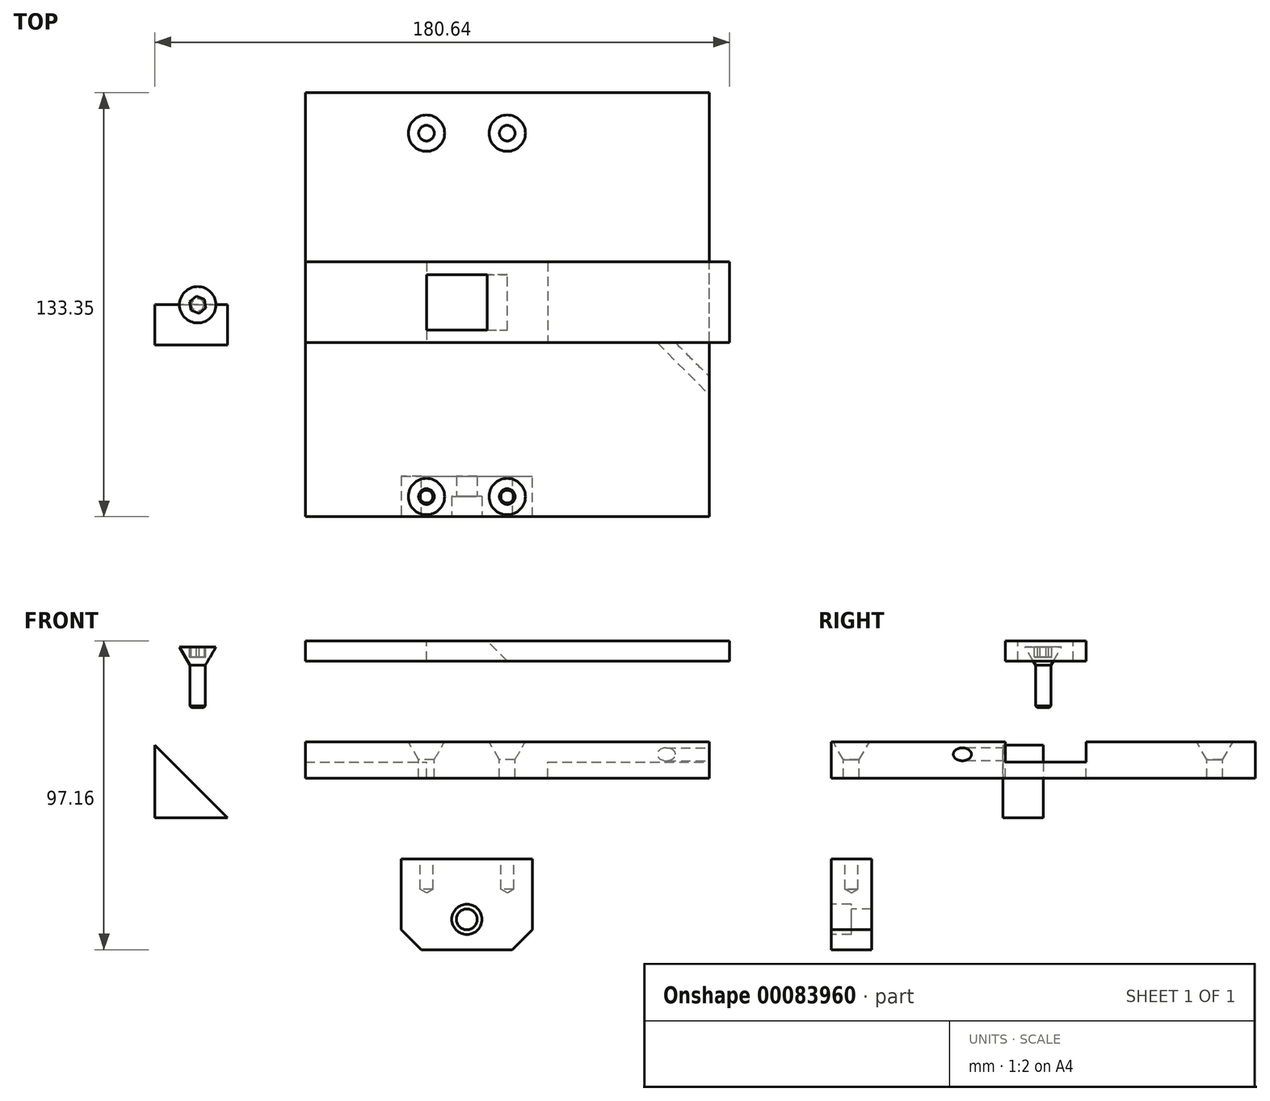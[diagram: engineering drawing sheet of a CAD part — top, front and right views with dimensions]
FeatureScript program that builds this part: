
annotation { "Feature Type Name" : "Feature", "Feature Type Description" : "" }
export const myFeature = defineFeature(function(context is Context, id is Id, definition is map)
    precondition{}
    {
        {
            var Q0;
            Q0=qCreatedBy(makeId("Top.planeOp"),FACE);
            var sketch = newSketch(context, id + "F0", { "sketchPlane" : qUnion([Q0])});
            skLineSegment(sketch, "E0.bottom", {"start": v(50.8, -66.68) * mm, "end": v(-50.8, -66.68) * mm});
            skLineSegment(sketch, "E0.top", {"start": v(50.8, 66.68) * mm, "end": v(-50.8, 66.68) * mm});
            skLineSegment(sketch, "E0.left", {"start": v(50.8, -66.68) * mm, "end": v(50.8, 66.68) * mm});
            skLineSegment(sketch, "E0.right", {"start": v(-50.8, -66.68) * mm, "end": v(-50.8, 66.68) * mm});
            skPoint(sketch, "E0.middle", {"position": v(0, 0) * mm});
            skSolve(sketch);
        }
        {
            var Q0;
            Q0=makeQuery(id+"F0.imprint","IMPRINT",FACE,{"disambiguationData":[TD([[makeQuery(id+"F0.imprint","IMPRINT",EDGE,{"derivedFrom":sQuery(id+"F0.wireOp",EDGE,"E0.bottom")}),-1.0]])]});
            extrude(context, id + "F1", {"entities" : qUnion([Q0]), "depth" : 11.43 * mm});
        }
        {
            var Q0;
            Q0=makeQuery(id+"F1.opExtrude","CAP_FACE",FACE,{"disambiguationData":[OSD([sQuery(id+"F0.wireOp",EDGE,"E0.bottom"),sQuery(id+"F0.wireOp",EDGE,"E0.top"),sQuery(id+"F0.wireOp",EDGE,"E0.left"),sQuery(id+"F0.wireOp",EDGE,"E0.right")])],"isStart":false});
            var sketch = newSketch(context, id + "F2", { "sketchPlane" : qUnion([Q0])});
            skLineSegment(sketch, "E1", {"start": v(-50.8, 53.98) * mm, "end": v(50.8, 53.98) * mm, "construction": true});
            skLineSegment(sketch, "E2", {"start": v(-50.8, -60.33) * mm, "end": v(50.8, -60.33) * mm, "construction": true});
            skLineSegment(sketch, "E3", {"start": v(-12.7, 66.68) * mm, "end": v(-12.7, -66.68) * mm, "construction": true});
            skLineSegment(sketch, "E4", {"start": v(12.7, 66.68) * mm, "end": v(12.7, -66.68) * mm, "construction": true});
            skPoint(sketch, "E5", {"position": v(-12.7, 53.98) * mm});
            skPoint(sketch, "E6", {"position": v(12.7, 53.98) * mm});
            skPoint(sketch, "E7", {"position": v(12.7, -60.33) * mm});
            skPoint(sketch, "E8", {"position": v(-12.7, -60.33) * mm});
            skSolve(sketch);
        }
        {
            var Q0;
            Q0=sQuery(id+"F2.wireOp",VERTEX,"E5");
            var Q1;
            Q1=sQuery(id+"F2.wireOp",VERTEX,"E6");
            var Q2;
            Q2=sQuery(id+"F2.wireOp",VERTEX,"E8");
            var Q3;
            Q3=sQuery(id+"F2.wireOp",VERTEX,"E7");
            var Q4;
            Q4=makeQuery(id+"F1.opExtrude","SWEPT_BODY",BODY,{"disambiguationData":[OSD([sQuery(id+"F0.wireOp",EDGE,"E0.bottom"),sQuery(id+"F0.wireOp",EDGE,"E0.top"),sQuery(id+"F0.wireOp",EDGE,"E0.left"),sQuery(id+"F0.wireOp",EDGE,"E0.right")])]});
            hole(context, id + "F3", {"style" : HoleStyle.C_SINK, "endStyle" : HoleEndStyle.THROUGH, "standardTappedOrClearance" : lookupTablePath({ "standard" : "ANSI", "size" : "#10 (0.2)", "type" : "Drilled" }), "standardBlindInLast" : lookupTablePath({ "standard" : "ANSI", "size" : "#10", "type" : "Drilled" }), "holeDiameter" : 4.9 * mm, "cSinkDiameter" : 11.43 * mm, "cSinkAngle" : 60 * degree, "locations" : qUnion([Q0, Q1, Q2, Q3]), "scope" : qUnion([Q4]), "isTappedThrough" : true});
        }
        {
            var Q0;
            Q0=makeQuery(id+"F1.opExtrude","CAP_FACE",FACE,{"disambiguationData":[OSD([sQuery(id+"F0.wireOp",EDGE,"E0.bottom"),sQuery(id+"F0.wireOp",EDGE,"E0.top"),sQuery(id+"F0.wireOp",EDGE,"E0.left"),sQuery(id+"F0.wireOp",EDGE,"E0.right")])],"isStart":true});
            cPlane(context, id + "F4", {"entities" : qUnion([Q0]), "cplaneType" : CPlaneType.OFFSET, "offset" : 25.4 * mm, "width" : 152.4 * mm, "height" : 152.4 * mm});
        }
        {
            var Q0;
            Q0=qCreatedBy(id+"F4.planeOp",FACE);
            var sketch = newSketch(context, id + "F5", { "sketchPlane" : qUnion([Q0])});
            skLineSegment(sketch, "E9.bottom", {"start": v(-20.64, 66.68) * mm, "end": v(20.64, 66.68) * mm});
            skLineSegment(sketch, "E9.top", {"start": v(-20.64, 53.98) * mm, "end": v(20.64, 53.98) * mm});
            skLineSegment(sketch, "E9.left", {"start": v(-20.64, 66.68) * mm, "end": v(-20.64, 53.98) * mm});
            skLineSegment(sketch, "E9.right", {"start": v(20.64, 66.68) * mm, "end": v(20.64, 53.98) * mm});
            skLineSegment(sketch, "E10", {"start": v(0, 66.68) * mm, "end": v(0, 53.98) * mm, "construction": true});
            skLineSegment(sketch, "E11", {"start": v(0, 66.68) * mm, "end": v(0, 24.97) * mm, "construction": true});
            skSolve(sketch);
        }
        {
            var Q0;
            Q0=makeQuery(id+"F5.imprint","IMPRINT",FACE,{"disambiguationData":[TD([[makeQuery(id+"F5.imprint","IMPRINT",EDGE,{"derivedFrom":sQuery(id+"F5.wireOp",EDGE,"E9.bottom")}),-1.0]])]});
            extrude(context, id + "F6", {"entities" : qUnion([Q0]), "depth" : 28.57 * mm});
        }
        {
            var Q0;
            Q0=qCreatedBy(id+"F4.planeOp",FACE);
            var sketch = newSketch(context, id + "F7", { "sketchPlane" : qUnion([Q0])});
            skPoint(sketch, "E12.0", {"position": v(-12.7, 60.33) * mm});
            skPoint(sketch, "E13.0", {"position": v(12.7, 60.33) * mm});
            skSolve(sketch);
        }
        {
            var Q0;
            Q0=sQuery(id+"F7.wireOp",VERTEX,"E12.0");
            var Q1;
            Q1=sQuery(id+"F7.wireOp",VERTEX,"E13.0");
            var Q2;
            Q2=makeQuery(id+"F6.opExtrude","SWEPT_BODY",BODY,{"disambiguationData":[OSD([sQuery(id+"F5.wireOp",EDGE,"E9.bottom"),sQuery(id+"F5.wireOp",EDGE,"E9.top"),sQuery(id+"F5.wireOp",EDGE,"E9.left"),sQuery(id+"F5.wireOp",EDGE,"E9.right")])]});
            hole(context, id + "F8", {"style" : HoleStyle.SIMPLE, "endStyle" : HoleEndStyle.BLIND, "oppositeDirection" : true, "standardTappedOrClearance" : lookupTablePath({ "standard" : "ANSI", "engagement" : "75%", "pitch" : "32 tpi", "size" : "#10", "type" : "Tapped" }), "standardBlindInLast" : lookupTablePath({ "standard" : "ANSI", "engagement" : "75%", "pitch" : "32 tpi", "size" : "#10", "type" : "Tapped" }), "holeDiameter" : 4.04 * mm, "holeDepth" : 9.52 * mm, "locations" : qUnion([Q0, Q1]), "scope" : qUnion([Q2]), "majorDiameter" : 4.83 * mm});
        }
        {
            var Q0;
            Q0=makeQuery(id+"F6.opExtrude","SWEPT_FACE",FACE,{"disambiguationData":[OSD([sQuery(id+"F5.wireOp",EDGE,"E9.bottom")])]});
            var sketch = newSketch(context, id + "F9", { "sketchPlane" : qUnion([Q0])});
            skLineSegment(sketch, "E14", {"start": v(0, -25.4) * mm, "end": v(0, -53.98) * mm, "construction": true});
            skLineSegment(sketch, "E15", {"start": v(-20.64, -44.44) * mm, "end": v(20.64, -44.44) * mm, "construction": true});
            skPoint(sketch, "E16", {"position": v(0, -44.44) * mm});
            skSolve(sketch);
        }
        {
            var Q0;
            Q0=sQuery(id+"F9.wireOp",VERTEX,"E16");
            var Q1;
            Q1=makeQuery(id+"F6.opExtrude","SWEPT_BODY",BODY,{"disambiguationData":[OSD([sQuery(id+"F5.wireOp",EDGE,"E9.bottom"),sQuery(id+"F5.wireOp",EDGE,"E9.top"),sQuery(id+"F5.wireOp",EDGE,"E9.left"),sQuery(id+"F5.wireOp",EDGE,"E9.right")])]});
            hole(context, id + "F10", {"style" : HoleStyle.C_BORE, "endStyle" : HoleEndStyle.THROUGH, "holeDiameter" : 6.53 * mm, "cBoreDiameter" : 9.52 * mm, "cBoreDepth" : 6.35 * mm, "locations" : qUnion([Q0]), "scope" : qUnion([Q1]), "isTappedThrough" : true});
        }
        {
            var Q0;
            Q0=makeQuery(id+"F2.imprint","IMPRINT",FACE,{"disambiguationData":[TD([[makeQuery(id+"F2.imprint","IMPRINT",EDGE,{"derivedFrom":makeQuery(id+"F1.opExtrude","CAP_EDGE",EDGE,{"disambiguationData":[OSD([sQuery(id+"F0.wireOp",EDGE,"E0.bottom")])],"isStart":false})}),-1.0]])]});
            var sketch = newSketch(context, id + "F11", { "sketchPlane" : qUnion([Q0])});
            skLineSegment(sketch, "E17.0.0", {"start": v(-12.7, -66.68) * mm, "end": v(12.7, -66.68) * mm, "construction": true});
            skCircle(sketch, "E17.0.1", {"center": v(12.7, -60.33) * mm, "radius": 5.71 * mm, "construction": true});
            skLineSegment(sketch, "E17.0.2", {"start": v(12.7, -66.68) * mm, "end": v(50.8, -66.68) * mm, "construction": true});
            skLineSegment(sketch, "E17.0.3", {"start": v(50.8, -66.68) * mm, "end": v(50.8, 66.68) * mm, "construction": true});
            skLineSegment(sketch, "E17.0.4", {"start": v(50.8, 66.68) * mm, "end": v(-50.8, 66.68) * mm, "construction": true});
            skLineSegment(sketch, "E17.0.5", {"start": v(-50.8, 66.68) * mm, "end": v(-50.8, -66.68) * mm, "construction": true});
            skLineSegment(sketch, "E17.0.6", {"start": v(-50.8, -66.68) * mm, "end": v(-12.7, -66.68) * mm, "construction": true});
            skCircle(sketch, "E17.0.7", {"center": v(-12.7, -60.33) * mm, "radius": 5.71 * mm, "construction": true});
            skLineSegment(sketch, "E18", {"start": v(-50.8, 13.46) * mm, "end": v(50.8, 13.46) * mm});
            skLineSegment(sketch, "E19", {"start": v(-50.8, -11.94) * mm, "end": v(50.8, -11.94) * mm});
            skLineSegment(sketch, "E20", {"start": v(-50.8, 0) * mm, "end": v(50.8, 0) * mm, "construction": true});
            skLineSegment(sketch, "E21", {"start": v(-12.7, 13.46) * mm, "end": v(-12.7, -11.94) * mm});
            skLineSegment(sketch, "E22", {"start": v(25.4, 13.46) * mm, "end": v(25.4, -11.94) * mm});
            skSolve(sketch);
        }
        {
            var Q0;
            {var subQ3=sQuery(id+"F11.wireOp",EDGE,"E21");Q0=makeQuery(id+"F11.imprint","IMPRINT",FACE,{"disambiguationData":[TD([[makeQuery(id+"F11.imprint","IMPRINT",EDGE,{"derivedFrom":subQ3}),-1.0]])]});}
            var Q1;
            {var subQ3=sQuery(id+"F11.wireOp",EDGE,"E22");Q1=makeQuery(id+"F11.imprint","IMPRINT",FACE,{"disambiguationData":[TD([[makeQuery(id+"F11.imprint","IMPRINT",EDGE,{"derivedFrom":subQ3}),1.0]])]});}
            extrude(context, id + "F12", {"entities" : qUnion([Q0, Q1]), "operationType" : NewBodyOperationType.REMOVE, "oppositeDirection" : true, "depth" : 6.35 * mm});
        }
        {
            var Q0;
            {var subQ0=sQuery(id+"F11.wireOp",EDGE,"E21");Q0=makeQuery(id+"F11.imprint","IMPRINT",FACE,{"disambiguationData":[TD([[makeQuery(id+"F11.imprint","IMPRINT",EDGE,{"derivedFrom":subQ0}),1.0]])]});}
            extrude(context, id + "F13", {"entities" : qUnion([Q0]), "operationType" : NewBodyOperationType.REMOVE, "endBound" : BoundingType.THROUGH_ALL, "oppositeDirection" : true, "depth" : 25.4 * mm});
        }
        {
            var Q0;
            {var subQ0=sQuery(id+"F0.wireOp",EDGE,"E0.right");var subQ1=sQuery(id+"F0.wireOp",EDGE,"E0.left");var subQ2=sQuery(id+"F0.wireOp",EDGE,"E0.bottom");Q0=makeQuery(id+"F13.boolean.opBoolean","SPLIT",FACE,{"disambiguationData":[TD([makeQuery(id+"F1.opExtrude","SWEPT_FACE",FACE,{"disambiguationData":[OSD([subQ2])]})])],"derivedFrom":makeQuery(id+"F1.opExtrude","CAP_FACE",FACE,{"disambiguationData":[OSD([subQ2,sQuery(id+"F0.wireOp",EDGE,"E0.top"),subQ1,subQ0])],"isStart":false})});}
            cPlane(context, id + "F14", {"entities" : qUnion([Q0]), "cplaneType" : CPlaneType.OFFSET, "offset" : 25.4 * mm, "width" : 152.4 * mm, "height" : 152.4 * mm});
        }
        {
            var Q0;
            Q0=qCreatedBy(id+"F14.planeOp",FACE);
            var sketch = newSketch(context, id + "F15", { "sketchPlane" : qUnion([Q0])});
            skLineSegment(sketch, "E23.0", {"start": v(-50.8, 13.46) * mm, "end": v(50.8, 13.46) * mm, "construction": true});
            skLineSegment(sketch, "E24.0", {"start": v(-50.8, -11.94) * mm, "end": v(50.8, -11.94) * mm, "construction": true});
            skLineSegment(sketch, "E25.0", {"start": v(-12.7, 13.46) * mm, "end": v(-12.7, -11.94) * mm, "construction": true});
            skLineSegment(sketch, "E26.0", {"start": v(25.4, 13.46) * mm, "end": v(25.4, -11.94) * mm, "construction": true});
            skLineSegment(sketch, "E27.0", {"start": v(50.8, -11.94) * mm, "end": v(50.8, 13.46) * mm, "construction": true});
            skLineSegment(sketch, "E28.bottom", {"start": v(-50.8, 13.46) * mm, "end": v(50.8, 13.46) * mm});
            skLineSegment(sketch, "E28.top", {"start": v(-50.8, -11.94) * mm, "end": v(50.8, -11.94) * mm});
            skLineSegment(sketch, "E28.left", {"start": v(-50.8, 13.46) * mm, "end": v(-50.8, -11.94) * mm});
            skLineSegment(sketch, "E28.right", {"start": v(50.8, 13.46) * mm, "end": v(50.8, -11.94) * mm});
            skSolve(sketch);
        }
        {
            var Q0;
            Q0=makeQuery(id+"F15.imprint","IMPRINT",FACE,{"disambiguationData":[TD([[makeQuery(id+"F15.imprint","IMPRINT",EDGE,{"derivedFrom":sQuery(id+"F15.wireOp",EDGE,"E28.bottom")}),-1.0]])]});
            extrude(context, id + "F16", {"entities" : qUnion([Q0]), "depth" : 6.35 * mm});
        }
        {
            var Q0;
            Q0=makeQuery(id+"F16.opExtrude","CAP_FACE",FACE,{"disambiguationData":[OSD([sQuery(id+"F15.wireOp",EDGE,"E28.bottom"),sQuery(id+"F15.wireOp",EDGE,"E28.top"),sQuery(id+"F15.wireOp",EDGE,"E28.left"),sQuery(id+"F15.wireOp",EDGE,"E28.right")])],"isStart":false});
            var sketch = newSketch(context, id + "F17", { "sketchPlane" : qUnion([Q0])});
            skLineSegment(sketch, "E29", {"start": v(-50.8, 9.5) * mm, "end": v(50.8, 9.5) * mm, "construction": true});
            skLineSegment(sketch, "E30", {"start": v(-50.8, -7.98) * mm, "end": v(50.8, -7.98) * mm, "construction": true});
            skLineSegment(sketch, "E31.bottom", {"start": v(-12.7, 9.5) * mm, "end": v(6.35, 9.5) * mm});
            skLineSegment(sketch, "E31.top", {"start": v(-12.7, -7.98) * mm, "end": v(6.35, -7.98) * mm});
            skLineSegment(sketch, "E31.left", {"start": v(-12.7, 9.5) * mm, "end": v(-12.7, -7.98) * mm});
            skLineSegment(sketch, "E31.right", {"start": v(6.35, 9.5) * mm, "end": v(6.35, -7.98) * mm});
            skSolve(sketch);
        }
        {
            var Q0;
            Q0=makeQuery(id+"F17.imprint","IMPRINT",FACE,{"disambiguationData":[TD([[makeQuery(id+"F17.imprint","IMPRINT",EDGE,{"derivedFrom":sQuery(id+"F17.wireOp",EDGE,"E31.bottom")}),-1.0]])]});
            extrude(context, id + "F18", {"entities" : qUnion([Q0]), "operationType" : NewBodyOperationType.REMOVE, "endBound" : BoundingType.THROUGH_ALL, "oppositeDirection" : true, "depth" : 25.4 * mm});
        }
        {
            var Q0;
            Q0=qCreatedBy(makeId("Front.planeOp"),FACE);
            var sketch = newSketch(context, id + "F19", { "sketchPlane" : qUnion([Q0])});
            skLineSegment(sketch, "E32", {"start": v(-98.1, 10.41) * mm, "end": v(-75.24, -12.44) * mm});
            skLineSegment(sketch, "E33", {"start": v(-75.24, -12.44) * mm, "end": v(-98.1, -12.44) * mm});
            skLineSegment(sketch, "E34", {"start": v(-98.1, -12.44) * mm, "end": v(-98.1, 10.41) * mm});
            skSolve(sketch);
        }
        {
            var Q0;
            Q0=makeQuery(id+"F19.imprint","IMPRINT",FACE,{"disambiguationData":[TD([[makeQuery(id+"F19.imprint","IMPRINT",EDGE,{"derivedFrom":sQuery(id+"F19.wireOp",EDGE,"E32")}),-1.0]])]});
            extrude(context, id + "F20", {"entities" : qUnion([Q0]), "depth" : 12.7 * mm});
        }
        {
            var Q0;
            Q0=makeQuery(id+"F18.boolean.opBoolean","INTERSECT",EDGE,{"derivedFrom":[makeQuery(id+"F16.opExtrude","CAP_FACE",FACE,{"disambiguationData":[OSD([sQuery(id+"F15.wireOp",EDGE,"E28.bottom"),sQuery(id+"F15.wireOp",EDGE,"E28.top"),sQuery(id+"F15.wireOp",EDGE,"E28.left"),sQuery(id+"F15.wireOp",EDGE,"E28.right")])],"isStart":true}),makeQuery(id+"F18.opExtrude","SWEPT_FACE",FACE,{"disambiguationData":[OSD([sQuery(id+"F17.wireOp",EDGE,"E31.right")])]})]});
            chamfer(context, id + "F21", {"entities" : qUnion([Q0]), "chamferType" : ChamferType.OFFSET_ANGLE, "width" : 6.35 * mm, "oppositeDirection" : false, "angle" : 45 * degree, "tangentPropagation" : true});
        }
        {
            var Q0;
            Q0=makeQuery(id+"F16.opExtrude","SWEPT_FACE",FACE,{"disambiguationData":[OSD([sQuery(id+"F15.wireOp",EDGE,"E28.right")])]});
            extrude(context, id + "F22", {"entities" : qUnion([Q0]), "operationType" : NewBodyOperationType.ADD, "depth" : 12.7 * mm});
        }
        {
            var Q0;
            Q0=makeQuery(id+"F1.opExtrude","SWEPT_FACE",FACE,{"disambiguationData":[OSD([sQuery(id+"F0.wireOp",EDGE,"E0.left")])]});
            extrude(context, id + "F23", {"entities" : qUnion([Q0]), "operationType" : NewBodyOperationType.ADD, "depth" : 25.4 * mm});
        }
        {
            var Q0;
            Q0=makeQuery(id+"F22.opExtrude","CAP_FACE",FACE,{"disambiguationData":[OSD([sQuery(id+"F15.wireOp",EDGE,"E28.right")])],"isStart":false});
            extrude(context, id + "F24", {"entities" : qUnion([Q0]), "operationType" : NewBodyOperationType.ADD, "depth" : 19.05 * mm});
        }
        {
            var Q0;
            Q0=makeQuery(id+"F6.opExtrude","CAP_EDGE",EDGE,{"disambiguationData":[OSD([sQuery(id+"F5.wireOp",EDGE,"E9.left")])],"isStart":false});
            var Q1;
            Q1=makeQuery(id+"F6.opExtrude","CAP_EDGE",EDGE,{"disambiguationData":[OSD([sQuery(id+"F5.wireOp",EDGE,"E9.right")])],"isStart":false});
            chamfer(context, id + "F25", {"entities" : qUnion([Q0, Q1]), "width" : 6.35 * mm, "tangentPropagation" : true});
        }
        {
            var Q0;
            Q0=makeQuery(id+"F23.opExtrude","CAP_EDGE",EDGE,{"disambiguationData":[OSD([sQuery(id+"F0.wireOp",EDGE,"E0.bottom"),sQuery(id+"F0.wireOp",EDGE,"E0.left")])],"isStart":false});
            var Q1;
            Q1=makeQuery(id+"F23.opExtrude","CAP_FACE",FACE,{"disambiguationData":[OSD([sQuery(id+"F0.wireOp",EDGE,"E0.left")])],"isStart":false});
            cPlane(context, id + "F26", {"entities" : qUnion([Q0, Q1]), "cplaneType" : CPlaneType.LINE_ANGLE, "offset" : 0 * mm, "angle" : 45 * degree, "width" : 152.4 * mm, "height" : 152.4 * mm});
        }
        {
            var Q0;
            Q0=qCreatedBy(id+"F26.planeOp",FACE);
            var sketch = newSketch(context, id + "F27", { "sketchPlane" : qUnion([Q0])});
            skLineSegment(sketch, "E35.0.0", {"start": v(-63.4, 5.08) * mm, "end": v(-45.44, 5.08) * mm});
            skLineSegment(sketch, "E35.0.1", {"start": v(-45.44, 5.08) * mm, "end": v(-45.44, 11.43) * mm});
            skLineSegment(sketch, "E35.0.2", {"start": v(-45.44, 11.43) * mm, "end": v(-6.74, 11.43) * mm});
            skLineSegment(sketch, "E35.0.3", {"start": v(-6.74, 11.43) * mm, "end": v(-6.74, 0) * mm});
            skLineSegment(sketch, "E35.0.4", {"start": v(-6.74, 0) * mm, "end": v(-101.03, 0) * mm});
            skLineSegment(sketch, "E35.0.5", {"start": v(-101.03, 0) * mm, "end": v(-101.03, 11.43) * mm});
            skLineSegment(sketch, "E35.0.6", {"start": v(-101.03, 11.43) * mm, "end": v(-63.4, 11.43) * mm});
            skLineSegment(sketch, "E35.0.7", {"start": v(-63.4, 11.43) * mm, "end": v(-63.4, 5.08) * mm});
            skLineSegment(sketch, "E36", {"start": v(-6.74, 7.47) * mm, "end": v(-45.44, 7.47) * mm, "construction": true});
            skLineSegment(sketch, "E37", {"start": v(-35.92, 11.43) * mm, "end": v(-35.92, 0) * mm, "construction": true});
            skPoint(sketch, "E38", {"position": v(-35.92, 7.47) * mm});
            skSolve(sketch);
        }
        {
            var Q0;
            Q0=sQuery(id+"F27.wireOp",VERTEX,"E38");
            var Q1;
            Q1=makeQuery(id+"F1.opExtrude","SWEPT_BODY",BODY,{"disambiguationData":[OSD([sQuery(id+"F0.wireOp",EDGE,"E0.bottom"),sQuery(id+"F0.wireOp",EDGE,"E0.top"),sQuery(id+"F0.wireOp",EDGE,"E0.left"),sQuery(id+"F0.wireOp",EDGE,"E0.right")])]});
            hole(context, id + "F28", {"style" : HoleStyle.SIMPLE, "endStyle" : HoleEndStyle.BLIND, "oppositeDirection" : true, "standardTappedOrClearance" : lookupTablePath({ "standard" : "ANSI", "engagement" : "75%", "pitch" : "32 tpi", "size" : "#10", "type" : "Tapped" }), "standardBlindInLast" : lookupTablePath({ "standard" : "ANSI", "engagement" : "75%", "pitch" : "32 tpi", "size" : "#10", "type" : "Tapped" }), "holeDiameter" : 4.04 * mm, "holeDepth" : 25.4 * mm, "locations" : qUnion([Q0]), "scope" : qUnion([Q1]), "majorDiameter" : 4.83 * mm});
        }
        {
            var Q0;
            Q0=qCreatedBy(makeId("Front.planeOp"),FACE);
            var sketch = newSketch(context, id + "F29", { "sketchPlane" : qUnion([Q0])});
            skLineSegment(sketch, "E39.bottom", {"start": v(-90.36, 41.21) * mm, "end": v(-84.64, 41.21) * mm});
            skLineSegment(sketch, "E39.top", {"start": v(-87.06, 22.16) * mm, "end": v(-84.64, 22.16) * mm});
            skLineSegment(sketch, "E40", {"start": v(-87.06, 35.5) * mm, "end": v(-87.06, 22.16) * mm});
            skLineSegment(sketch, "E41", {"start": v(-84.64, 41.21) * mm, "end": v(-84.64, 22.16) * mm, "construction": true});
            skLineSegment(sketch, "E42", {"start": v(-90.36, 41.21) * mm, "end": v(-87.06, 35.5) * mm});
            skLineSegment(sketch, "E43", {"start": v(-84.64, 41.21) * mm, "end": v(-84.64, 22.16) * mm});
            skSolve(sketch);
        }
        {
            var Q0;
            Q0=makeQuery(id+"F29.imprint","IMPRINT",FACE,{"disambiguationData":[TD([[makeQuery(id+"F29.imprint","IMPRINT",EDGE,{"derivedFrom":sQuery(id+"F29.wireOp",EDGE,"E39.bottom")}),-1.0]])]});
            var Q1;
            Q1=sQuery(id+"F29.wireOp",EDGE,"E43");
            revolve(context, id + "F30", {"entities" : qUnion([Q0]), "axis" : qUnion([Q1]), "revolveType" : RevolveType.FULL});
        }
        {
            var Q0;
            Q0=makeQuery(id+"F30.opRevolve","SWEPT_EDGE",EDGE,{"disambiguationData":[OSD([sQuery(id+"F29.wireOp",EDGE,"E39.top"),sQuery(id+"F29.wireOp",EDGE,"E40")])]});
            chamfer(context, id + "F31", {"entities" : qUnion([Q0]), "width" : 0.5 * mm, "tangentPropagation" : true});
        }
        {
            var Q0;
            Q0=makeQuery(id+"F30.opRevolve","SWEPT_FACE",FACE,{"disambiguationData":[OSD([sQuery(id+"F29.wireOp",EDGE,"E39.bottom")])]});
            var sketch = newSketch(context, id + "F32", { "sketchPlane" : qUnion([Q0])});
            skCircle(sketch, "E44.0.0", {"center": v(-84.64, 0) * mm, "radius": 5.71 * mm, "construction": true});
            skCircle(sketch, "E45.cCircle", {"center": v(-84.64, 0) * mm, "radius": 2.37 * mm, "construction": true});
            skLineSegment(sketch, "E45.0", {"start": v(-82.07, -0.95) * mm, "end": v(-84.18, -2.7) * mm});
            skLineSegment(sketch, "E45.1", {"start": v(-84.18, -2.7) * mm, "end": v(-86.75, -1.75) * mm});
            skLineSegment(sketch, "E45.2", {"start": v(-86.75, -1.75) * mm, "end": v(-87.22, 0.95) * mm});
            skLineSegment(sketch, "E45.3", {"start": v(-87.22, 0.95) * mm, "end": v(-85.1, 2.7) * mm});
            skLineSegment(sketch, "E45.4", {"start": v(-85.1, 2.7) * mm, "end": v(-82.54, 1.75) * mm});
            skLineSegment(sketch, "E45.5", {"start": v(-82.54, 1.75) * mm, "end": v(-82.07, -0.95) * mm});
            skPoint(sketch, "E45.0.midPoint", {"position": v(-83.12, -1.83) * mm});
            skSolve(sketch);
        }
        {
            var Q0;
            Q0=makeQuery(id+"F32.imprint","IMPRINT",FACE,{"disambiguationData":[TD([[makeQuery(id+"F32.imprint","IMPRINT",EDGE,{"derivedFrom":sQuery(id+"F32.wireOp",EDGE,"E45.0")}),-1.0]])]});
            extrude(context, id + "F33", {"entities" : qUnion([Q0]), "operationType" : NewBodyOperationType.REMOVE, "oppositeDirection" : true, "depth" : 3.17 * mm});
        }
    });
